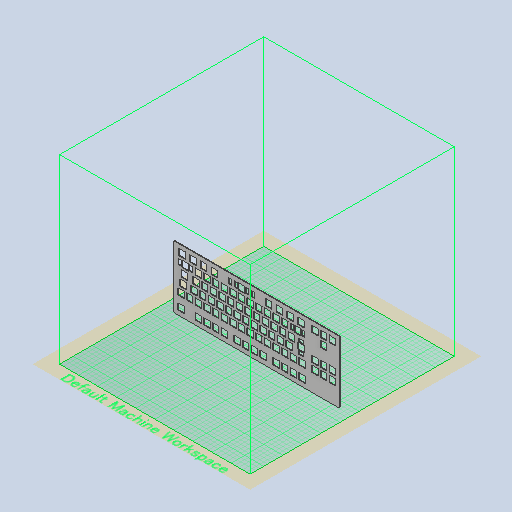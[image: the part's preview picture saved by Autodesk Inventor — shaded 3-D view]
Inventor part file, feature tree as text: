
AUTODESK INVENTOR PART (.ipt)
format: ipt  version: 2022 (Build 260153000, 153)  size: 3,646,464 bytes
history: native  units: mm
features: sketch x23, hole x15, extrude x9, fillet x3, other x1, chamfer x1
ambient origin geometry x8: Origin, YZ Plane, XZ Plane, XY Plane, X Axis, Y Axis, Z Axis, Center Point
bodies: Body1 (feature_tree), Body2 (feature_tree)
feature tree (52):
  other  "ソリッド1"
  extrude  "押し出し1"  Depth=3.46mm
  extrude  "押し出し2"  Depth=13.9954mm
  extrude  "押し出し3"  Depth=13.9954mm
  extrude  "押し出し4"  Depth=0.254mm
  extrude  "押し出し5"  Depth=19.05mm
  hole  "穴1"  [1 undecoded]
  sketch  "スケッチ10"
  sketch  "スケッチ11"
  sketch  "スケッチ12"
  sketch  "スケッチ13"
  sketch  "スケッチ14"
  sketch  "スケッチ15"
  sketch  "スケッチ16"
  sketch  "スケッチ17"
  sketch  "スケッチ18"
  sketch  "スケッチ19"
  sketch  "スケッチ20"
  sketch  "スケッチ21"
  sketch  "スケッチ22"
  hole  "穴2"  [1 undecoded]
  hole  "穴3"  [1 undecoded]
  hole  "穴4"  [1 undecoded]
  hole  "穴5"  [1 undecoded]
  hole  "穴6"  [1 undecoded]
  hole  "穴7"  [1 undecoded]
  hole  "穴8"  [1 undecoded]
  hole  "穴9"  [1 undecoded]
  hole  "穴10"  [1 undecoded]
  hole  "穴11"  [1 undecoded]
  hole  "穴12"  [1 undecoded]
  hole  "穴13"  [1 undecoded]
  hole  "穴14"  [1 undecoded]
  hole  "穴15"  [1 undecoded]
  fillet  "フィレット6"  Radius=19.05mm
  extrude  "押し出し8"  Depth=13.9954mm TaperAngle=0.0deg
  extrude  "押し出し9"  Depth=21.2725mm
  fillet  "フィレット9"  Radius=13.9954mm
  chamfer  "面取り4"  Distance=110.0mm
  extrude  "押し出し11"  Depth=54.61mm
  fillet  "フィレット10"  Radius=19.05mm
  extrude  "押し出し12"  Depth=26.035mm
  sketch  "スケッチ2"
  sketch  "スケッチ3"
  sketch  "スケッチ4"
  sketch  "スケッチ5"
  sketch  "スケッチ6"
  sketch  "スケッチ23"
  sketch  "スケッチ26"
  sketch  "スケッチ27"
  sketch  "スケッチ29"
  sketch  "スケッチ30"
note: 15 required parameter values undecoded (feature->parameter linkage not recoverable at this tier; creation-order binding heuristic only, values carry confidence <= 0.55)
